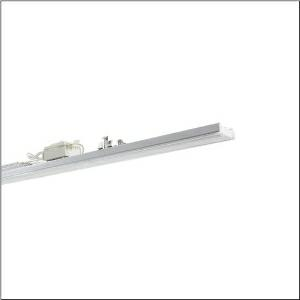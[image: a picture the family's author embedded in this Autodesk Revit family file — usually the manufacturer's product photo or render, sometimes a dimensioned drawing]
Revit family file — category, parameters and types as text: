
# Revit family: licross_r__21_recessed_mo_52tl12cn49xg_563f
name_source: partatom
category: Lighting Fixtures
units: mm (PartAtom-declared; Revit-internal decimal feet)

## family parameters
Cut with Voids When Loaded = No
Host = Face
Light Source = No
Part Type = Normal
Room Calculation Point = No
Round Connector Dimension = Use Diameter
Shared = No

## types (1)
- --- (1 x LED, 9260 lm, 49.9 W, 4000K)
    Apparent Load = 50 VA
    CIE Flux Codes = 72 92 99 100 100
    Color Rendering = 80
    Color Temperature = 4000K
    Default Elevation = 1800 mm
    Description = Licross® 21 Recessed MO, luminaire insert, of sheet steel, galvanised, coil coated, white, length: 1.500mm, width: 66mm, height: 67mm, LED rated luminous flux: 9.260lm, light colour: 840, control gear: ON/OFF Multilumen, CLOi, control gear: ECG Multilumen, with plug, 3-pole, with phase selection, mains connection: 220..240V, AC, 50/60Hz, start of lifetime: 50W, end of service life: 61W, internal wiring halogen-free, primary optical cover: cover, of PMMA, light emission: direct distribution, primary light characteristic: symmetric, protection rating (complete): IP40, insulation class (complete): insulation class I (protective earthing), certification: CE, ENEC, VDE, UKCA, protection symbol: D if used in an environment without relevant dust loads with corresponding accessories, impact resistance: IK06, permissible ambient temperature for indoor applications: -35..+40°C, corresponds to IFS (International Featured Standards) requirements for safety and quality in the food industry, reducing of maximum allowable ambient temperature of 5°C with ceiling mounting, LABS conformity tested according to VDMA 24364:2018-05, packaging unit: 1 piece
    Height = 58 mm
    Lamp = 1 x LED
    Lamp Light Flux = 9260 lm
    Lamp Power = 49.9 W
    Lamp count = 1
    Length = 1500 mm
    Luminous efficacy = 186 lm/W
    Manufacturer = Siteco
    ModVariant = No
    Model = 52TL12CN49XG
    Mounting Place = Ceiling
    Mounting Type = Pendant
    Number of Poles = 1
    OnlyDefault = Yes
    Power Factor = 1
    Product Name = Licross® 21 Recessed MO
    Product group = luminaire insert | ceiling pendant
    ProductGroupID = 902
    Protection Class = Protection class I
    Protection Degree = IP 40
    RLX_Detail_Level = 1
    RLX_Emergency_Light_Flux = 0 lm
    RLX_Emergency_Type = 0
    RLX_Emergency_Type_DB = No
    RlxData = <blob elided: 22401 chars, md5=0c4a1d30>
    Socket = socket
    Standby Power = 0 W
    System Light Flux = 9260 lm
    System Power = 50 W
    Type Comments = factory setting: luminous flux: 100 % | (A | C | E) | 116 mA
    Type Image = l_1296930.jpg
    URL = http://relux.com
    VarID = @adj_132087
    Voltage = 0 V
    Weight = 0.00 kg
    Width = 66 mm

## geometry (parser evidence)
native form markers: Blend x4, Sweep x11
no freeform markers — native parametric forms only
